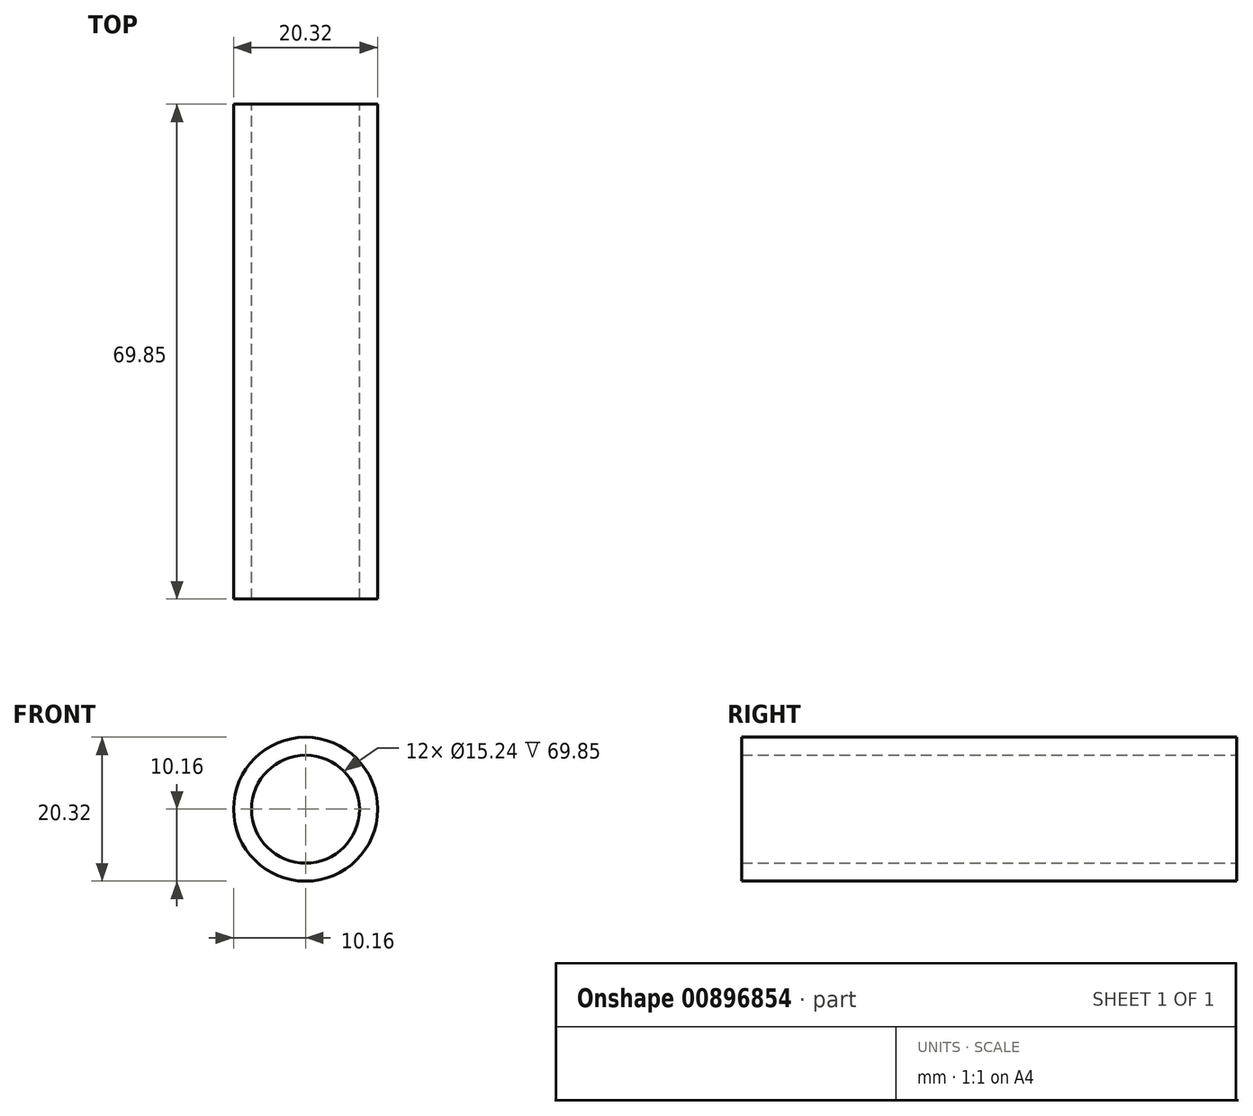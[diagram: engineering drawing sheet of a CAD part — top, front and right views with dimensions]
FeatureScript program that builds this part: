
annotation { "Feature Type Name" : "Feature", "Feature Type Description" : "" }
export const myFeature = defineFeature(function(context is Context, id is Id, definition is map)
    precondition{}
    {
        {
            var Q0;
            Q0=qCreatedBy(makeId("Front.planeOp"),FACE);
            var sketch = newSketch(context, id + "F0", { "sketchPlane" : qUnion([Q0])});
            skCircle(sketch, "E0", {"center": v(0, 0) * mm, "radius": 10.16 * mm});
            skCircle(sketch, "E1", {"center": v(0, 0) * mm, "radius": 7.62 * mm});
            skSolve(sketch);
        }
        {
            var Q0;
            Q0=makeQuery(id+"F0.imprint","IMPRINT",FACE,{"disambiguationData":[TD([[makeQuery(id+"F0.imprint","IMPRINT",EDGE,{"derivedFrom":sQuery(id+"F0.wireOp",EDGE,"E0")}),1.0]])]});
            extrude(context, id + "F1", {"entities" : qUnion([Q0]), "depth" : 69.85 * mm, "offsetDistance" : 25.4 * mm});
        }
    });
